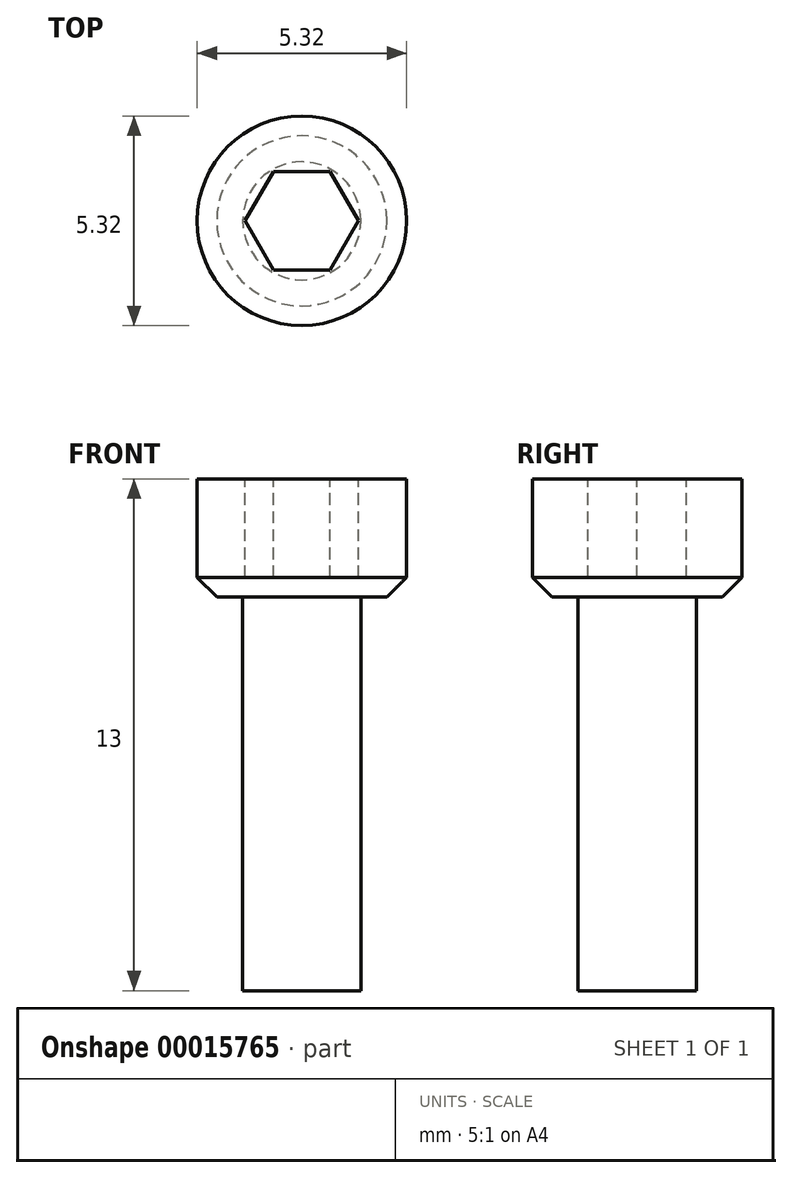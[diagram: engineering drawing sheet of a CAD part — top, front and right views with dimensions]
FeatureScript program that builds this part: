
annotation { "Feature Type Name" : "Feature", "Feature Type Description" : "" }
export const myFeature = defineFeature(function(context is Context, id is Id, definition is map)
    precondition{}
    {
        {
            var Q0;
            Q0=qCreatedBy(makeId("Top.planeOp"),FACE);
            var sketch = newSketch(context, id + "F0", { "sketchPlane" : qUnion([Q0])});
            skCircle(sketch, "E0", {"center": v(0, 0) * mm, "radius": 2.66 * mm});
            skSolve(sketch);
        }
        {
            var Q0;
            Q0 = qSketchRegion(id + "F0", true);
            extrude(context, id + "F1", {"entities" : qUnion([Q0]), "depth" : 3 * mm});
        }
        {
            var Q0;
            Q0=makeQuery(id+"F1.opExtrude","CAP_FACE",FACE,{"disambiguationData":[OSD([sQuery(id+"F0.wireOp",EDGE,"E0")])],"isStart":true});
            var sketch = newSketch(context, id + "F2", { "sketchPlane" : qUnion([Q0])});
            skCircle(sketch, "E1", {"center": v(0, 0) * mm, "radius": 1.5 * mm});
            skSolve(sketch);
        }
        {
            var Q0;
            Q0 = qSketchRegion(id + "F2", true);
            extrude(context, id + "F3", {"entities" : qUnion([Q0]), "operationType" : NewBodyOperationType.ADD, "depth" : 10 * mm});
        }
        {
            var Q0;
            Q0=makeQuery(id+"F1.opExtrude","CAP_FACE",FACE,{"disambiguationData":[OSD([sQuery(id+"F0.wireOp",EDGE,"E0")])],"isStart":false});
            var sketch = newSketch(context, id + "F4", { "sketchPlane" : qUnion([Q0])});
            skCircle(sketch, "E2.cCircle", {"center": v(0, 0) * mm, "radius": 1.25 * mm, "construction": true});
            skLineSegment(sketch, "E2.0", {"start": v(-0.72, 1.25) * mm, "end": v(0.72, 1.25) * mm});
            skLineSegment(sketch, "E2.1", {"start": v(0.72, 1.25) * mm, "end": v(1.44, 0) * mm});
            skLineSegment(sketch, "E2.2", {"start": v(1.44, 0) * mm, "end": v(0.72, -1.25) * mm});
            skLineSegment(sketch, "E2.3", {"start": v(0.72, -1.25) * mm, "end": v(-0.72, -1.25) * mm});
            skLineSegment(sketch, "E2.4", {"start": v(-0.72, -1.25) * mm, "end": v(-1.44, 0) * mm});
            skLineSegment(sketch, "E2.5", {"start": v(-1.44, 0) * mm, "end": v(-0.72, 1.25) * mm});
            skPoint(sketch, "E2.0.midPoint", {"position": v(0, 1.25) * mm});
            skSolve(sketch);
        }
        {
            var Q0;
            Q0 = qSketchRegion(id + "F4", true);
            extrude(context, id + "F5", {"entities" : qUnion([Q0]), "operationType" : NewBodyOperationType.REMOVE, "oppositeDirection" : true, "depth" : 2.5 * mm});
        }
        {
            var Q0;
            Q0=makeQuery(id+"F1.opExtrude","CAP_EDGE",EDGE,{"disambiguationData":[OSD([sQuery(id+"F0.wireOp",EDGE,"E0")])],"isStart":true});
            chamfer(context, id + "F6", {"entities" : qUnion([Q0]), "width" : .5 * mm, "tangentPropagation" : true});
        }
    });
